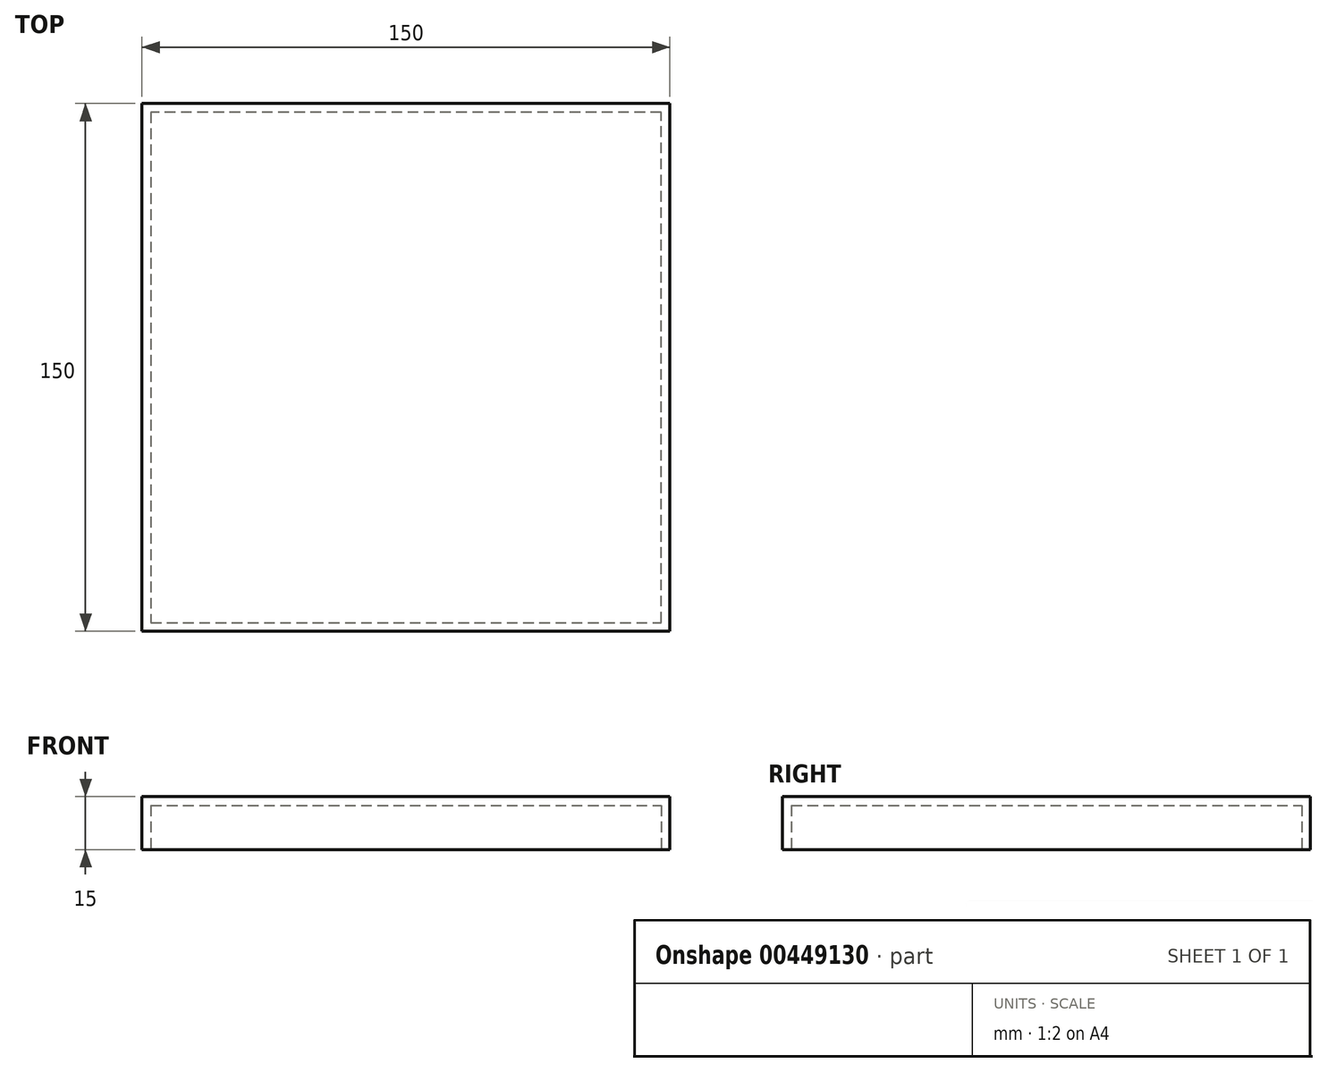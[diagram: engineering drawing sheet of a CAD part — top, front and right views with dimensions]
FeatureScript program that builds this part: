
annotation { "Feature Type Name" : "Feature", "Feature Type Description" : "" }
export const myFeature = defineFeature(function(context is Context, id is Id, definition is map)
    precondition{}
    {
        {
            var Q0;
            Q0=qCreatedBy(makeId("Top.planeOp"),FACE);
            var sketch = newSketch(context, id + "F0", { "sketchPlane" : qUnion([Q0])});
            skLineSegment(sketch, "E0.bottom", {"start": v(0, -75) * mm, "end": v(0, -75) * mm});
            skLineSegment(sketch, "E0.top", {"start": v(0, 0) * mm, "end": v(0, 0) * mm});
            skLineSegment(sketch, "E1.top", {"start": v(0, -103.2) * mm, "end": v(0, -103.2) * mm});
            skLineSegment(sketch, "E2", {"start": v(0, -75) * mm, "end": v(75, -75) * mm});
            skLineSegment(sketch, "E3", {"start": v(75, -75) * mm, "end": v(75, 0) * mm});
            skLineSegment(sketch, "E4", {"start": v(75, 0) * mm, "end": v(75, 75) * mm});
            skLineSegment(sketch, "E5", {"start": v(75, 75) * mm, "end": v(0, 75) * mm});
            skLineSegment(sketch, "E6", {"start": v(0, 75) * mm, "end": v(-75, 75) * mm});
            skLineSegment(sketch, "E7", {"start": v(-75, 75) * mm, "end": v(-75, 0) * mm});
            skLineSegment(sketch, "E8", {"start": v(-75, 0) * mm, "end": v(-75, -75) * mm});
            skLineSegment(sketch, "E9", {"start": v(-75, -75) * mm, "end": v(0, -75) * mm});
            skSolve(sketch);
        }
        {
            var Q0;
            Q0 = qSketchRegion(id + "F0", true);
            extrude(context, id + "F1", {"entities" : qUnion([Q0]), "depth" : 15 * mm});
        }
        {
            var Q0;
            Q0=makeQuery(id+"F1.opExtrude","CAP_FACE",FACE,{"disambiguationData":[OSD([sQuery(id+"F0.wireOp",EDGE,"E2"),sQuery(id+"F0.wireOp",EDGE,"E3"),sQuery(id+"F0.wireOp",EDGE,"E4"),sQuery(id+"F0.wireOp",EDGE,"E5"),sQuery(id+"F0.wireOp",EDGE,"E6"),sQuery(id+"F0.wireOp",EDGE,"E7"),sQuery(id+"F0.wireOp",EDGE,"E8"),sQuery(id+"F0.wireOp",EDGE,"E9")])],"isStart":true});
            shell(context, id + "F2", {"entities" : qUnion([Q0]), "thickness" : 2.5 * mm});
        }
    });
